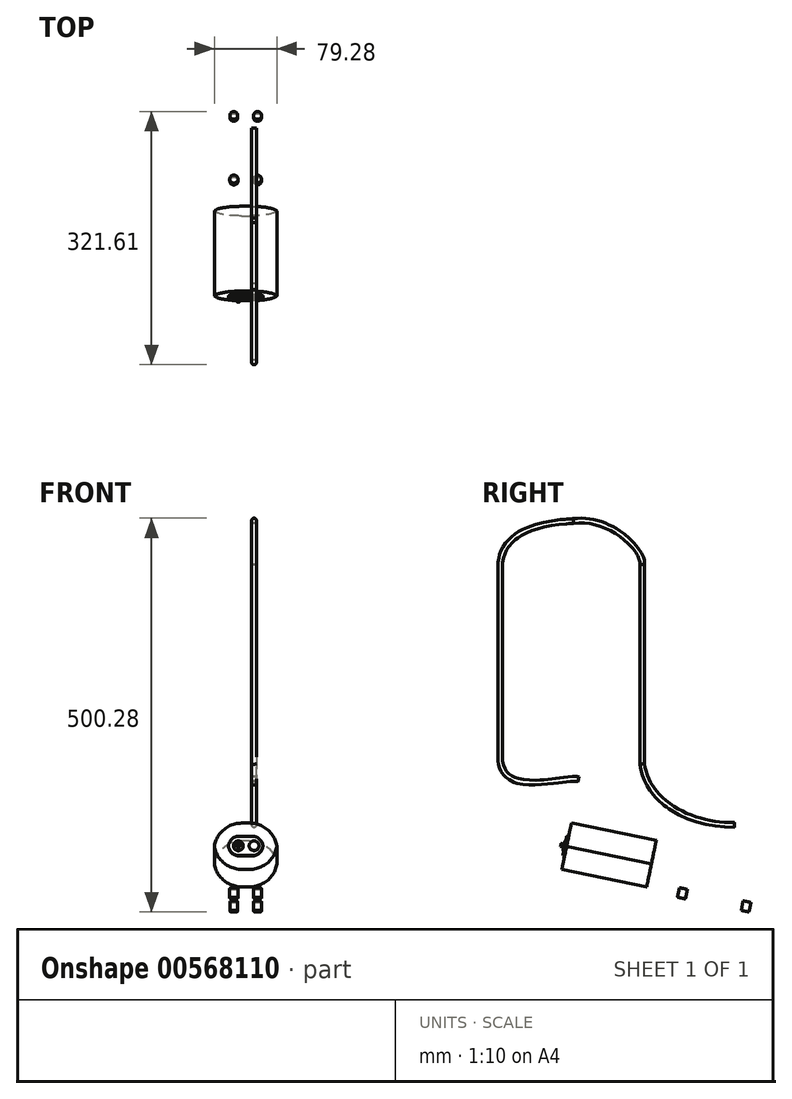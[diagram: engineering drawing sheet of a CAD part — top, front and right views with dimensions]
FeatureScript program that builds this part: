
annotation { "Feature Type Name" : "Feature", "Feature Type Description" : "" }
export const myFeature = defineFeature(function(context is Context, id is Id, definition is map)
    precondition{}
    {
        {
            var Q0;
            Q0=qCreatedBy(makeId("Top.planeOp"),FACE);
            var sketch = newSketch(context, id + "F0", { "sketchPlane" : qUnion([Q0])});
            skCircle(sketch, "E0", {"center": v(0, 0) * mm, "radius": 3 * mm});
            skSolve(sketch);
        }
        {
            var Q0;
            Q0=qCreatedBy(makeId("Right.planeOp"),FACE);
            var sketch = newSketch(context, id + "F1", { "sketchPlane" : qUnion([Q0])});
            skFitSpline(sketch, "E1", {"points": [v(0, 0) * mm, v(93.07, 58.78) * mm], "startDerivative": vector(0, 167.68) * mm, "endDerivative": vector(48.36, 3.77) * mm});
            skFitSpline(sketch, "E2", {"points": [v(93.07, 58.78) * mm, v(180.44, 3.47) * mm], "startDerivative": vector(141.73, 18.32) * mm, "endDerivative": vector(-7.68, -55.68) * mm});
            skLineSegment(sketch, "E3", {"start": v(180.44, 3.47) * mm, "end": v(180.44, -249.9) * mm});
            skFitSpline(sketch, "E4", {"points": [v(180.44, -249.9) * mm, v(297.38, -327.2) * mm], "startDerivative": vector(19.76, -148.2) * mm, "endDerivative": vector(166.21, 1.57) * mm});
            skLineSegment(sketch, "E5", {"start": v(0, 0) * mm, "end": v(0, -241) * mm});
            skFitSpline(sketch, "E6", {"points": [v(0, -241) * mm, v(99.47, -269.2) * mm], "startDerivative": vector(0, -159.62) * mm, "endDerivative": vector(61.41, -12.67) * mm});
            skSolve(sketch);
        }
        {
            var Q0;
            Q0=makeQuery(id+"F0.imprint","IMPRINT",FACE,{"disambiguationData":[TD([[makeQuery(id+"F0.imprint","IMPRINT",EDGE,{"derivedFrom":sQuery(id+"F0.wireOp",EDGE,"E0")}),1.0]])]});
            var Q1;
            Q1=sQuery(id+"F0.wireOp",EDGE,"E0");
            var Q2;
            Q2=sQuery(id+"F1.wireOp",EDGE,"E1");
            var Q3;
            Q3=sQuery(id+"F1.wireOp",EDGE,"E2");
            var Q4;
            Q4=sQuery(id+"F1.wireOp",EDGE,"E3");
            var Q5;
            Q5=sQuery(id+"F1.wireOp",EDGE,"E4");
            var Q6;
            Q6=sQuery(id+"F1.wireOp",EDGE,"E5");
            var Q7;
            Q7=sQuery(id+"F1.wireOp",EDGE,"E6");
            sweep(context, id + "F2", {"profiles" : qUnion([Q0]), "surfaceProfiles" : qUnion([Q1]), "path" : qUnion([Q2, Q3, Q4, Q5, Q6, Q7])});
        }
        {
            var Q0;
            Q0=makeQuery(id+"F2.opSweep","CAP_FACE",FACE,{"disambiguationData":[OSD([sQuery(id+"F0.wireOp",EDGE,"E0"),sQuery(id+"F1.wireOp",VERTEX,"E4.end")])],"isStart":false});
            var sketch = newSketch(context, id + "F3", { "sketchPlane" : qUnion([Q0])});
            skLineSegment(sketch, "E7.bottom", {"start": v(40, -359.99) * mm, "end": v(-40, -359.99) * mm});
            skLineSegment(sketch, "E7.top", {"start": v(40, -299.99) * mm, "end": v(-40, -299.99) * mm});
            skLineSegment(sketch, "E7.left", {"start": v(-40, -359.99) * mm, "end": v(-40, -299.99) * mm});
            skLineSegment(sketch, "E7.right", {"start": v(40, -359.99) * mm, "end": v(40, -299.99) * mm});
            skPoint(sketch, "E7.middle", {"position": v(0, -329.99) * mm});
            skCircle(sketch, "E8", {"center": v(0, -329.99) * mm, "radius": 6.23 * mm});
            skCircle(sketch, "E9", {"center": v(20, -329.99) * mm, "radius": 6.25 * mm});
            skLineSegment(sketch, "E10", {"start": v(-11.23, -329.99) * mm, "end": v(-11.23, -317.49) * mm});
            skLineSegment(sketch, "E11", {"start": v(-11.23, -317.49) * mm, "end": v(32.5, -317.49) * mm});
            skLineSegment(sketch, "E12", {"start": v(32.5, -317.49) * mm, "end": v(32.5, -342.49) * mm});
            skLineSegment(sketch, "E13", {"start": v(32.5, -342.49) * mm, "end": v(-11.23, -342.49) * mm});
            skLineSegment(sketch, "E14", {"start": v(-11.23, -342.49) * mm, "end": v(-11.23, -329.99) * mm});
            skCircle(sketch, "E15", {"center": v(20, -329.99) * mm, "radius": 2 * mm});
            skSolve(sketch);
        }
        {
            var Q0;
            Q0=makeQuery(id+"F3.imprint","IMPRINT",FACE,{"disambiguationData":[TD([[makeQuery(id+"F3.imprint","IMPRINT",EDGE,{"derivedFrom":sQuery(id+"F3.wireOp",EDGE,"E8")}),1.0]])]});
            extrude(context, id + "F4", {"entities" : qUnion([Q0]), "oppositeDirection" : true, "depth" : 1 * mm, "offsetDistance" : 25 * mm});
        }
        {
            var Q0;
            Q0=makeQuery(id+"F3.imprint","IMPRINT",FACE,{"disambiguationData":[TD([[makeQuery(id+"F3.imprint","IMPRINT",EDGE,{"derivedFrom":sQuery(id+"F3.wireOp",EDGE,"E8")}),1.0]])]});
            var Q1;
            Q1=makeQuery(id+"F3.imprint","IMPRINT",FACE,{"disambiguationData":[TD([[makeQuery(id+"F3.imprint","IMPRINT",EDGE,{"derivedFrom":sQuery(id+"F3.wireOp",EDGE,"E8")}),-1.0]])]});
            var Q2;
            Q2=makeQuery(id+"F3.imprint","IMPRINT",FACE,{"disambiguationData":[TD([[makeQuery(id+"F3.imprint","IMPRINT",EDGE,{"derivedFrom":sQuery(id+"F3.wireOp",EDGE,"E9")}),1.0]])]});
            extrude(context, id + "F5", {"entities" : qUnion([Q0, Q1, Q2]), "operationType" : NewBodyOperationType.ADD, "depth" : 2.5 * mm, "offsetDistance" : 25 * mm});
        }
        {
            var Q0;
            Q0=makeQuery(id+"F3.imprint","IMPRINT",FACE,{"disambiguationData":[TD([[makeQuery(id+"F3.imprint","IMPRINT",EDGE,{"derivedFrom":sQuery(id+"F3.wireOp",EDGE,"E9")}),1.0]])]});
            extrude(context, id + "F6", {"entities" : qUnion([Q0]), "operationType" : NewBodyOperationType.ADD, "oppositeDirection" : true, "depth" : 1 * mm, "offsetDistance" : 25 * mm});
        }
        {
            var Q0;
            Q0=makeQuery(id+"F3.imprint","IMPRINT",FACE,{"disambiguationData":[TD([[makeQuery(id+"F3.imprint","IMPRINT",EDGE,{"derivedFrom":sQuery(id+"F3.wireOp",EDGE,"E15")}),1.0]])]});
            extrude(context, id + "F7", {"entities" : qUnion([Q0]), "operationType" : NewBodyOperationType.ADD, "oppositeDirection" : true, "depth" : 5 * mm, "offsetDistance" : 25 * mm});
        }
        {
            var Q0;
            Q0=makeQuery(id+"F5.opExtrude","CAP_FACE",FACE,{"disambiguationData":[OSD([sQuery(id+"F0.wireOp",EDGE,"E0"),sQuery(id+"F1.wireOp",VERTEX,"E4.end"),sQuery(id+"F3.wireOp",EDGE,"E10"),sQuery(id+"F3.wireOp",EDGE,"E11"),sQuery(id+"F3.wireOp",EDGE,"E12"),sQuery(id+"F3.wireOp",EDGE,"E13"),sQuery(id+"F3.wireOp",EDGE,"E14"),sQuery(id+"F3.wireOp",EDGE,"E15")])],"isStart":false});
            var sketch = newSketch(context, id + "F8", { "sketchPlane" : qUnion([Q0])});
            skLineSegment(sketch, "E16", {"start": v(10.63, -317.49) * mm, "end": v(10.63, -342.49) * mm});
            skLineSegment(sketch, "E17", {"start": v(10.63, -329.99) * mm, "end": v(14.63, -329.99) * mm});
            skLineSegment(sketch, "E18.bottom", {"start": v(50.63, -359.99) * mm, "end": v(-29.37, -359.99) * mm});
            skLineSegment(sketch, "E18.top", {"start": v(50.63, -299.99) * mm, "end": v(-29.37, -299.99) * mm});
            skLineSegment(sketch, "E18.left", {"start": v(50.63, -359.99) * mm, "end": v(50.63, -299.99) * mm});
            skLineSegment(sketch, "E18.right", {"start": v(-29.37, -359.99) * mm, "end": v(-29.37, -299.99) * mm});
            skPoint(sketch, "E18.middle", {"position": v(10.63, -329.99) * mm});
            skSolve(sketch);
        }
        {
            var Q0;
            Q0=makeQuery(id+"F8.imprint","IMPRINT",FACE,{"disambiguationData":[TD([[makeQuery(id+"F8.imprint","IMPRINT",EDGE,{"derivedFrom":sQuery(id+"F8.wireOp",EDGE,"E18.bottom")}),-1.0]])]});
            var Q1;
            {var subQ0=makeQuery(id+"F5.opExtrude","CAP_EDGE",EDGE,{"disambiguationData":[OSD([sQuery(id+"F3.wireOp",EDGE,"E10"),sQuery(id+"F3.wireOp",EDGE,"E14")])],"isStart":false});Q1=makeQuery(id+"F8.imprint","IMPRINT",FACE,{"disambiguationData":[TD([[makeQuery(id+"F8.imprint","IMPRINT",EDGE,{"derivedFrom":subQ0}),-1.0]])]});}
            var Q2;
            {var subQ0=makeQuery(id+"F5.opExtrude","CAP_EDGE",EDGE,{"disambiguationData":[OSD([sQuery(id+"F3.wireOp",EDGE,"E12")])],"isStart":false});Q2=makeQuery(id+"F8.imprint","IMPRINT",FACE,{"disambiguationData":[TD([[makeQuery(id+"F8.imprint","IMPRINT",EDGE,{"derivedFrom":subQ0}),-1.0]])]});}
            var Q3;
            Q3=makeQuery(id+"F8.imprint","IMPRINT",FACE,{"disambiguationData":[TD([[makeQuery(id+"F8.imprint","IMPRINT",EDGE,{"derivedFrom":makeQuery(id+"F5.opExtrude","CAP_EDGE",EDGE,{"disambiguationData":[OSD([sQuery(id+"F3.wireOp",EDGE,"E15")])],"isStart":false})}),1.0]])]});
            var Q4;
            Q4=makeQuery(id+"F8.imprint","IMPRINT",FACE,{"disambiguationData":[TD([[makeQuery(id+"F8.imprint","IMPRINT",EDGE,{"derivedFrom":makeQuery(id+"F5.opExtrude","CAP_EDGE",EDGE,{"disambiguationData":[OSD([sQuery(id+"F0.wireOp",EDGE,"E0"),sQuery(id+"F1.wireOp",VERTEX,"E4.end")])],"isStart":false})}),1.0]])]});
            extrude(context, id + "F9", {"entities" : qUnion([Q0, Q1, Q2, Q3, Q4]), "operationType" : NewBodyOperationType.ADD, "depth" : 110 * mm, "offsetDistance" : 25 * mm});
        }
        {
            var Q0;
            Q0=makeQuery(id+"F5.opExtrude","SWEPT_EDGE",EDGE,{"disambiguationData":[OSD([sQuery(id+"F3.wireOp",EDGE,"E11"),sQuery(id+"F3.wireOp",EDGE,"E12")])]});
            var Q1;
            Q1=makeQuery(id+"F5.opExtrude","SWEPT_EDGE",EDGE,{"disambiguationData":[OSD([sQuery(id+"F3.wireOp",EDGE,"E12"),sQuery(id+"F3.wireOp",EDGE,"E13")])]});
            var Q2;
            Q2=makeQuery(id+"F5.opExtrude","SWEPT_EDGE",EDGE,{"disambiguationData":[OSD([sQuery(id+"F3.wireOp",EDGE,"E13"),sQuery(id+"F3.wireOp",EDGE,"E14")])]});
            var Q3;
            Q3=makeQuery(id+"F5.opExtrude","SWEPT_EDGE",EDGE,{"disambiguationData":[OSD([sQuery(id+"F3.wireOp",EDGE,"E10"),sQuery(id+"F3.wireOp",EDGE,"E11")])]});
            fillet(context, id + "F10", {"entities" : qUnion([Q0, Q1, Q2, Q3]), "radius" : 13.5 * mm, "tangentPropagation" : true, "allowEdgeOverflow" : false});
        }
        {
            var Q0;
            Q0=makeQuery(id+"F9.opExtrude","SWEPT_EDGE",EDGE,{"disambiguationData":[OSD([sQuery(id+"F8.wireOp",EDGE,"E18.top"),sQuery(id+"F8.wireOp",EDGE,"E18.left")])]});
            var Q1;
            Q1=makeQuery(id+"F9.opExtrude","SWEPT_EDGE",EDGE,{"disambiguationData":[OSD([sQuery(id+"F8.wireOp",EDGE,"E18.bottom"),sQuery(id+"F8.wireOp",EDGE,"E18.left")])]});
            var Q2;
            Q2=makeQuery(id+"F9.opExtrude","SWEPT_EDGE",EDGE,{"disambiguationData":[OSD([sQuery(id+"F8.wireOp",EDGE,"E18.top"),sQuery(id+"F8.wireOp",EDGE,"E18.right")])]});
            var Q3;
            Q3=makeQuery(id+"F9.opExtrude","SWEPT_EDGE",EDGE,{"disambiguationData":[OSD([sQuery(id+"F8.wireOp",EDGE,"E18.bottom"),sQuery(id+"F8.wireOp",EDGE,"E18.right")])]});
            fillet(context, id + "F11", {"entities" : qUnion([Q0, Q1, Q2, Q3]), "radius" : 35 * mm, "tangentPropagation" : true, "allowEdgeOverflow" : false});
        }
        {
            var Q0;
            Q0=makeQuery(id+"F9.opExtrude","SWEPT_FACE",FACE,{"disambiguationData":[OSD([sQuery(id+"F8.wireOp",EDGE,"E18.bottom")])]});
            var sketch = newSketch(context, id + "F12", { "sketchPlane" : qUnion([Q0])});
            skLineSegment(sketch, "E19", {"start": v(-15.63, -351.78) * mm, "end": v(-15.63, -296.78) * mm});
            skLineSegment(sketch, "E20", {"start": v(-15.63, -351.78) * mm, "end": v(-15.63, -406.78) * mm});
            skLineSegment(sketch, "E21", {"start": v(-15.63, -324.28) * mm, "end": v(-5.63, -324.28) * mm});
            skLineSegment(sketch, "E22", {"start": v(-15.63, -324.28) * mm, "end": v(-15.63, -296.78) * mm});
            skLineSegment(sketch, "E23", {"start": v(-15.63, -310.53) * mm, "end": v(-25.63, -310.53) * mm});
            skLineSegment(sketch, "E24", {"start": v(-15.63, -310.53) * mm, "end": v(-5.63, -310.53) * mm});
            skLineSegment(sketch, "E25", {"start": v(-5.63, -310.53) * mm, "end": v(4.37, -310.53) * mm});
            skCircle(sketch, "E26", {"center": v(-25.63, -310.53) * mm, "radius": 5.21 * mm});
            skCircle(sketch, "E27", {"center": v(4.37, -310.53) * mm, "radius": 5.02 * mm});
            skLineSegment(sketch, "E28", {"start": v(-15.63, -379.28) * mm, "end": v(-15.63, -406.78) * mm});
            skLineSegment(sketch, "E29", {"start": v(-15.63, -393.03) * mm, "end": v(-25.73, -393.03) * mm});
            skLineSegment(sketch, "E30", {"start": v(-25.73, -393.03) * mm, "end": v(4.45, -393.03) * mm});
            skCircle(sketch, "E31", {"center": v(4.45, -393.03) * mm, "radius": 5.05 * mm});
            skCircle(sketch, "E32", {"center": v(-25.73, -393.03) * mm, "radius": 5.05 * mm});
            skSolve(sketch);
        }
        {
            var Q0;
            Q0=makeQuery(id+"F12.imprint","IMPRINT",FACE,{"disambiguationData":[TD([[makeQuery(id+"F12.imprint","IMPRINT",EDGE,{"derivedFrom":sQuery(id+"F12.wireOp",EDGE,"E31")}),1.0]])]});
            var Q1;
            Q1=makeQuery(id+"F12.imprint","IMPRINT",FACE,{"disambiguationData":[TD([[makeQuery(id+"F12.imprint","IMPRINT",EDGE,{"derivedFrom":sQuery(id+"F12.wireOp",EDGE,"E32")}),1.0]])]});
            var Q2;
            Q2=makeQuery(id+"F12.imprint","IMPRINT",FACE,{"disambiguationData":[TD([[makeQuery(id+"F12.imprint","IMPRINT",EDGE,{"derivedFrom":sQuery(id+"F12.wireOp",EDGE,"E27")}),1.0]])]});
            var Q3;
            Q3=makeQuery(id+"F12.imprint","IMPRINT",FACE,{"disambiguationData":[TD([[makeQuery(id+"F12.imprint","IMPRINT",EDGE,{"derivedFrom":sQuery(id+"F12.wireOp",EDGE,"E26")}),1.0]])]});
            extrude(context, id + "F13", {"entities" : qUnion([Q0, Q1, Q2, Q3]), "operationType" : NewBodyOperationType.ADD, "depth" : 5 * mm, "offsetDistance" : 25 * mm, "hasSecondDirection" : true, "secondDirectionOppositeDirection" : true, "secondDirectionDepth" : 7.4 * mm});
        }
    });
